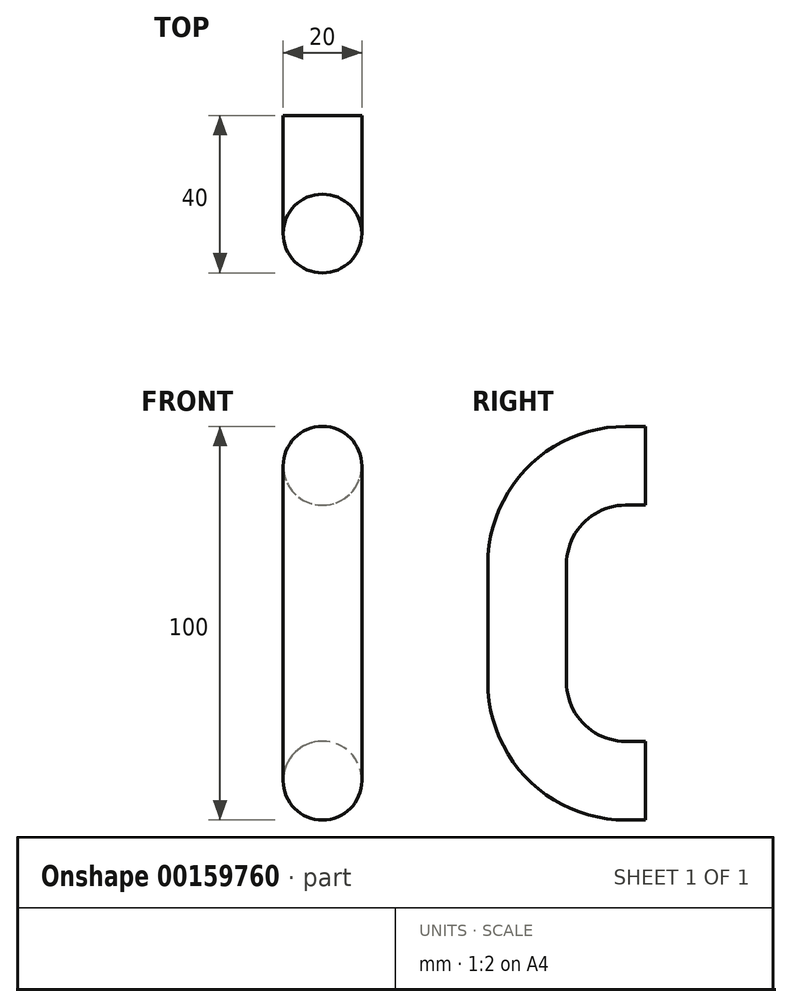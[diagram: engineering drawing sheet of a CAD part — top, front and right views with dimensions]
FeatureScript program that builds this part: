
annotation { "Feature Type Name" : "Feature", "Feature Type Description" : "" }
export const myFeature = defineFeature(function(context is Context, id is Id, definition is map)
    precondition{}
    {
        {
            var Q0;
            Q0=qCreatedBy(makeId("Front.planeOp"),FACE);
            var sketch = newSketch(context, id + "F0", { "sketchPlane" : qUnion([Q0])});
            skCircle(sketch, "E0", {"center": v(0, 0) * mm, "radius": 10 * mm});
            skSolve(sketch);
        }
        {
            var Q0;
            Q0=qCreatedBy(makeId("Right.planeOp"),FACE);
            var sketch = newSketch(context, id + "F1", { "sketchPlane" : qUnion([Q0])});
            skLineSegment(sketch, "E1", {"start": v(0, 0) * mm, "end": v(-5, 0) * mm});
            skLineSegment(sketch, "E2", {"start": v(-30, -25) * mm, "end": v(-30, -55) * mm});
            skLineSegment(sketch, "E3", {"start": v(-5, -80) * mm, "end": v(0, -80) * mm});
            skPoint(sketch, "E4.visualSharp", {"position": v(-30, 0) * mm});
            skArc(sketch, "E4.filletArc", {"start": v(-5, 0) * mm, "mid": v(-22.68, -7.32) * mm, "end": v(-30, -25) * mm});
            skPoint(sketch, "E5.visualSharp", {"position": v(-30, -80) * mm});
            skArc(sketch, "E5.filletArc", {"start": v(-30, -55) * mm, "mid": v(-22.68, -72.68) * mm, "end": v(-5, -80) * mm});
            skSolve(sketch);
        }
        {
            var Q0;
            Q0=makeQuery(id+"F0.imprint","IMPRINT",FACE,{"disambiguationData":[TD([[makeQuery(id+"F0.imprint","IMPRINT",EDGE,{"derivedFrom":sQuery(id+"F0.wireOp",EDGE,"E0")}),1.0]])]});
            var Q1;
            Q1 = qConstructionFilter(qBodyType(qCreatedBy(id + "F1" ,EDGE), BodyType.WIRE), ConstructionObject.NO);
            sweep(context, id + "F2", {"profiles" : qUnion([Q0]), "path" : qUnion([Q1])});
        }
    });
